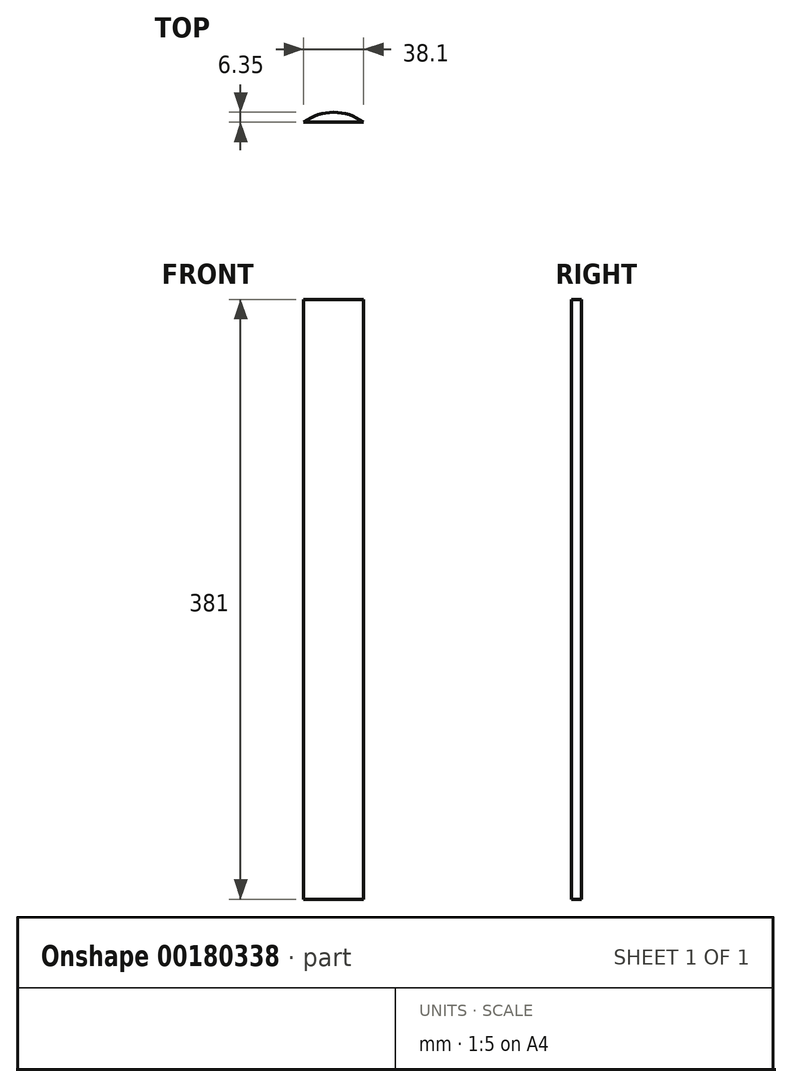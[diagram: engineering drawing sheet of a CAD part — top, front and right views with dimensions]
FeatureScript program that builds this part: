
annotation { "Feature Type Name" : "Feature", "Feature Type Description" : "" }
export const myFeature = defineFeature(function(context is Context, id is Id, definition is map)
    precondition{}
    {
        {
            var Q0;
            Q0=qCreatedBy(makeId("Top.planeOp"),FACE);
            var sketch = newSketch(context, id + "F0", { "sketchPlane" : qUnion([Q0])});
            skLineSegment(sketch, "E0.top", {"start": v(19.05, -6.35) * mm, "end": v(-19.05, -6.35) * mm});
            skPoint(sketch, "E0.middle", {"position": v(0, 0) * mm});
            skArc(sketch, "E1", {"start": v(19.05, -6.35) * mm, "mid": v(0, 0) * mm, "end": v(-19.05, -6.35) * mm});
            skSolve(sketch);
        }
        {
            var Q0;
            Q0=qSketchRegion(id+"F0",true);
            extrude(context, id + "F1", {"entities" : qUnion([Q0]), "depth" : 381 * mm});
        }
    });
